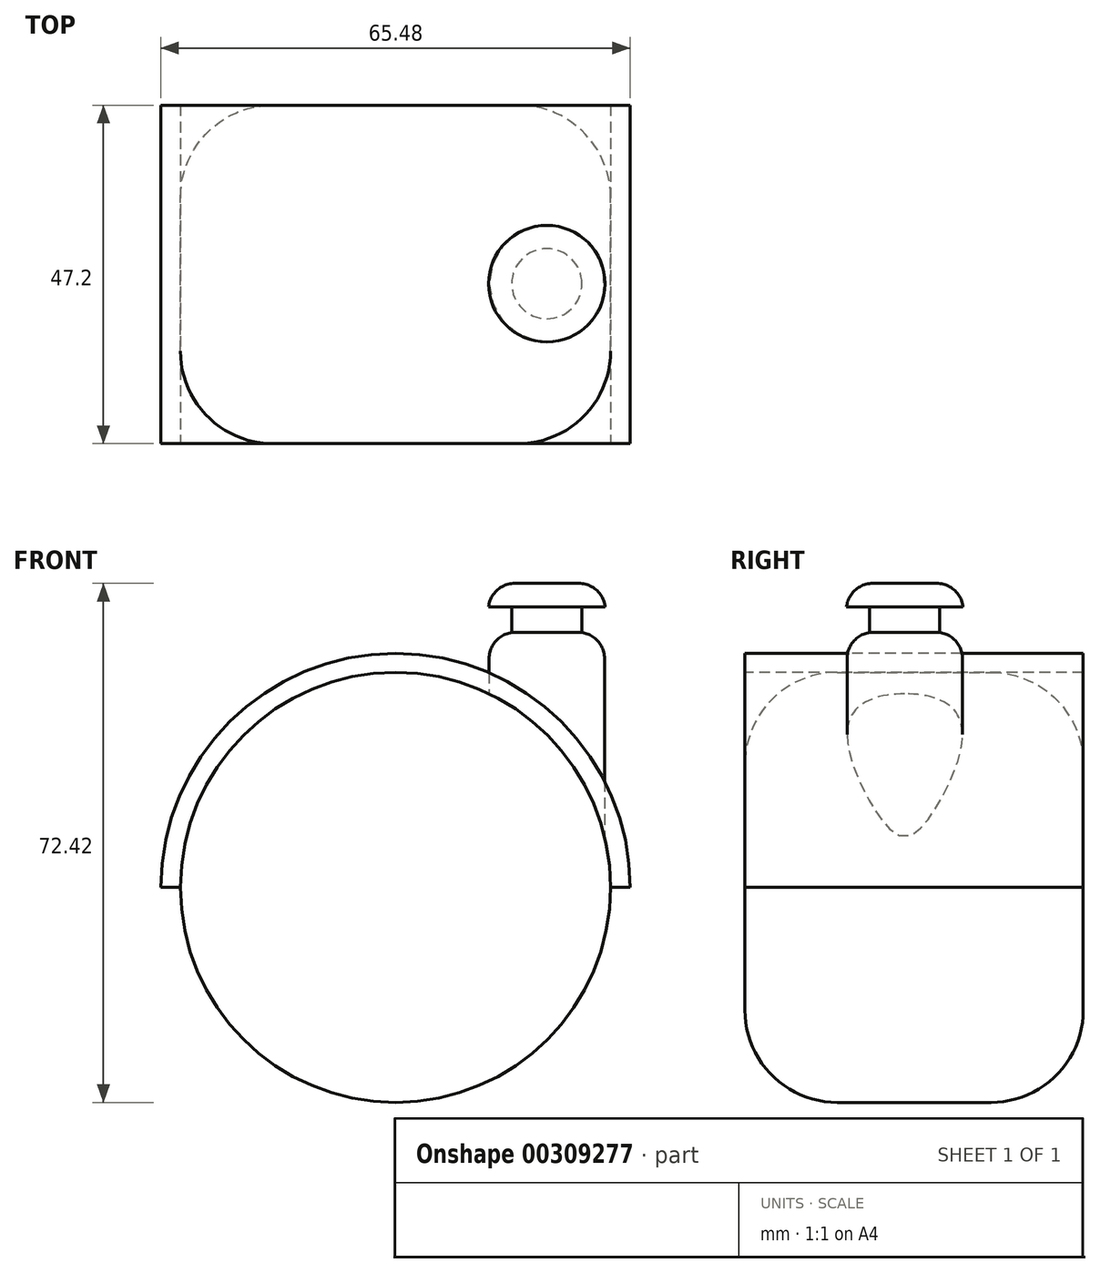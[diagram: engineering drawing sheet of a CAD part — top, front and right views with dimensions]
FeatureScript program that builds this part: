
annotation { "Feature Type Name" : "Feature", "Feature Type Description" : "" }
export const myFeature = defineFeature(function(context is Context, id is Id, definition is map)
    precondition{}
    {
        {
            var Q0;
            Q0=qCreatedBy(makeId("Front.planeOp"),FACE);
            var sketch = newSketch(context, id + "F0", { "sketchPlane" : qUnion([Q0])});
            skCircle(sketch, "E0", {"center": v(0, 0) * mm, "radius": 30 * mm});
            skSolve(sketch);
        }
        {
            var Q0;
            Q0=makeQuery(id+"F0.imprint","IMPRINT",FACE,{"disambiguationData":[TD([[makeQuery(id+"F0.imprint","IMPRINT",EDGE,{"derivedFrom":sQuery(id+"F0.wireOp",EDGE,"E0")}),1.0]])]});
            extrude(context, id + "F1", {"entities" : qUnion([Q0]), "depth" : 47.2 * mm});
        }
        {
            var Q0;
            Q0=makeQuery(id+"F1.opExtrude","CAP_FACE",FACE,{"disambiguationData":[OSD([sQuery(id+"F0.wireOp",EDGE,"E0")])],"isStart":false});
            var sketch = newSketch(context, id + "F2", { "sketchPlane" : qUnion([Q0])});
            skLineSegment(sketch, "E1", {"start": v(-30, 0) * mm, "end": v(-32.74, 0) * mm});
            skLineSegment(sketch, "E2", {"start": v(30, 0) * mm, "end": v(32.74, 0) * mm});
            skLineSegment(sketch, "E3", {"start": v(0, 30) * mm, "end": v(0, 32.74) * mm});
            skArc(sketch, "E4", {"start": v(32.74, 0) * mm, "mid": v(0, 32.74) * mm, "end": v(-32.74, 0) * mm});
            skArc(sketch, "E5", {"start": v(30, 0) * mm, "mid": v(0, 30) * mm, "end": v(-30, 0) * mm});
            skSolve(sketch);
        }
        {
            var Q0;
            Q0 = qSketchRegion(id + "F2", true);
            var Q1;
            Q1=sQuery(id+"F2.wireOp",EDGE,"E1");
            var Q2;
            Q2=sQuery(id+"F2.wireOp",EDGE,"E5");
            var Q3;
            Q3=sQuery(id+"F2.wireOp",EDGE,"E4");
            var Q4;
            Q4=sQuery(id+"F2.wireOp",EDGE,"E2");
            extrude(context, id + "F3", {"entities" : qUnion([Q0]), "bodyType" : ToolBodyType.SURFACE, "operationType" : NewBodyOperationType.ADD, "surfaceEntities" : qUnion([Q1, Q2, Q3, Q4]), "oppositeDirection" : true, "depth" : 47.2 * mm});
        }
        {
            var Q0;
            Q0=qCreatedBy(makeId("Top.planeOp"),FACE);
            var sketch = newSketch(context, id + "F4", { "sketchPlane" : qUnion([Q0])});
            skCircle(sketch, "E6", {"center": v(21.1, -24.9) * mm, "radius": 8.05 * mm});
            skSolve(sketch);
        }
        {
            var Q0;
            Q0 = qSketchRegion(id + "F4", true);
            extrude(context, id + "F5", {"entities" : qUnion([Q0]), "operationType" : NewBodyOperationType.ADD, "depth" : 35.56 * mm});
        }
        {
            var Q0;
            Q0=makeQuery(id+"F5.opExtrude","CAP_FACE",FACE,{"disambiguationData":[OSD([sQuery(id+"F4.wireOp",EDGE,"E6")])],"isStart":false});
            var sketch = newSketch(context, id + "F6", { "sketchPlane" : qUnion([Q0])});
            skCircle(sketch, "E7", {"center": v(21.1, -24.9) * mm, "radius": 4.89 * mm});
            skSolve(sketch);
        }
        {
            var Q0;
            Q0 = qSketchRegion(id + "F6", true);
            extrude(context, id + "F7", {"entities" : qUnion([Q0]), "operationType" : NewBodyOperationType.ADD, "depth" : 3.56 * mm});
        }
        {
            var Q0;
            Q0=makeQuery(id+"F7.opExtrude","CAP_FACE",FACE,{"disambiguationData":[OSD([sQuery(id+"F6.wireOp",EDGE,"E7")])],"isStart":false});
            var sketch = newSketch(context, id + "F8", { "sketchPlane" : qUnion([Q0])});
            skCircle(sketch, "E8", {"center": v(21.1, -24.9) * mm, "radius": 8.13 * mm});
            skSolve(sketch);
        }
        {
            var Q0;
            Q0 = qSketchRegion(id + "F8", true);
            extrude(context, id + "F9", {"entities" : qUnion([Q0]), "operationType" : NewBodyOperationType.ADD, "depth" : 3.3 * mm});
        }
        {
            var Q0;
            Q0=makeQuery(id+"F1.opExtrude","CAP_FACE",FACE,{"disambiguationData":[OSD([sQuery(id+"F0.wireOp",EDGE,"E0")])],"isStart":false});
            var sketch = newSketch(context, id + "F10", { "sketchPlane" : qUnion([Q0])});
            skArc(sketch, "E9", {"start": v(30, 0) * mm, "mid": v(0, 30) * mm, "end": v(-30, 0) * mm});
            skLineSegment(sketch, "E10", {"start": v(-30, 0) * mm, "end": v(-32.74, 0) * mm});
            skLineSegment(sketch, "E11", {"start": v(30, 0) * mm, "end": v(32.74, 0) * mm});
            skArc(sketch, "E12", {"start": v(32.74, 0) * mm, "mid": v(0, 32.66) * mm, "end": v(-32.74, 0) * mm});
            skSolve(sketch);
        }
        {
            var Q0;
            Q0 = qSketchRegion(id + "F10", true);
            extrude(context, id + "F11", {"entities" : qUnion([Q0]), "oppositeDirection" : true, "depth" : 47.2 * mm});
        }
        {
            var Q0;
            Q0=makeQuery(id+"F1.opExtrude","CAP_FACE",FACE,{"disambiguationData":[OSD([sQuery(id+"F0.wireOp",EDGE,"E0")])],"isStart":true});
            var Q1;
            Q1=makeQuery(id+"F1.opExtrude","CAP_FACE",FACE,{"disambiguationData":[OSD([sQuery(id+"F0.wireOp",EDGE,"E0")])],"isStart":false});
            fillet(context, id + "F12", {"entities" : qUnion([Q0, Q1]), "radius" : 12.88 * mm, "tangentPropagation" : true, "allowEdgeOverflow" : false});
        }
        {
            var Q0;
            Q0=makeQuery(id+"F5.opExtrude","CAP_EDGE",EDGE,{"disambiguationData":[OSD([sQuery(id+"F4.wireOp",EDGE,"E6")])],"isStart":false});
            fillet(context, id + "F13", {"entities" : qUnion([Q0]), "radius" : 3.68 * mm, "tangentPropagation" : true, "allowEdgeOverflow" : false});
        }
        {
            var Q0;
            Q0=makeQuery(id+"F9.opExtrude","CAP_FACE",FACE,{"disambiguationData":[OSD([sQuery(id+"F8.wireOp",EDGE,"E8")])],"isStart":false});
            fillet(context, id + "F14", {"entities" : qUnion([Q0]), "radius" : 3.68 * mm, "tangentPropagation" : true, "allowEdgeOverflow" : false});
        }
    });
